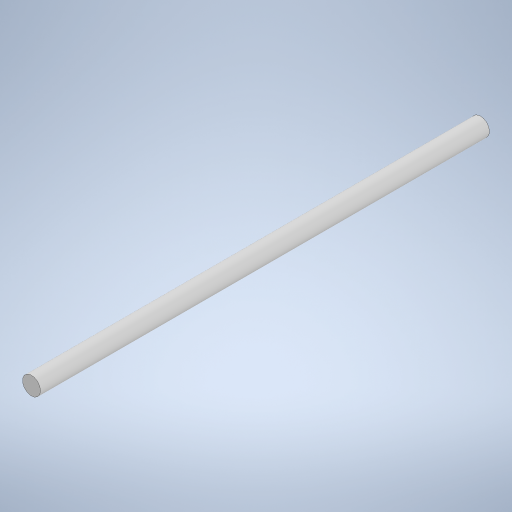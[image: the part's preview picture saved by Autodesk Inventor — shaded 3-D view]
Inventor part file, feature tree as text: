
AUTODESK INVENTOR PART (.ipt)
format: ipt  version: 2023 (Build 270158000, 158)  size: 232,448 bytes
history: native  units: in
note: dims shown in document units (in); Inventor stores cm internally (conversion verified against a paired STEP export)
features: extrude x1, sketch x1
ambient origin geometry x8: Origin, YZ Plane, XZ Plane, XY Plane, X Axis, Y Axis, Z Axis, Center Point
bodies: Solid1 (feature_tree)
feature tree (2):
  extrude  "Extrusion1"  Depth=56.0in TaperAngle=0.0deg
  sketch  "Sketch1"  dims[d0=2.25in d1=56.0in d2=0.0in]
